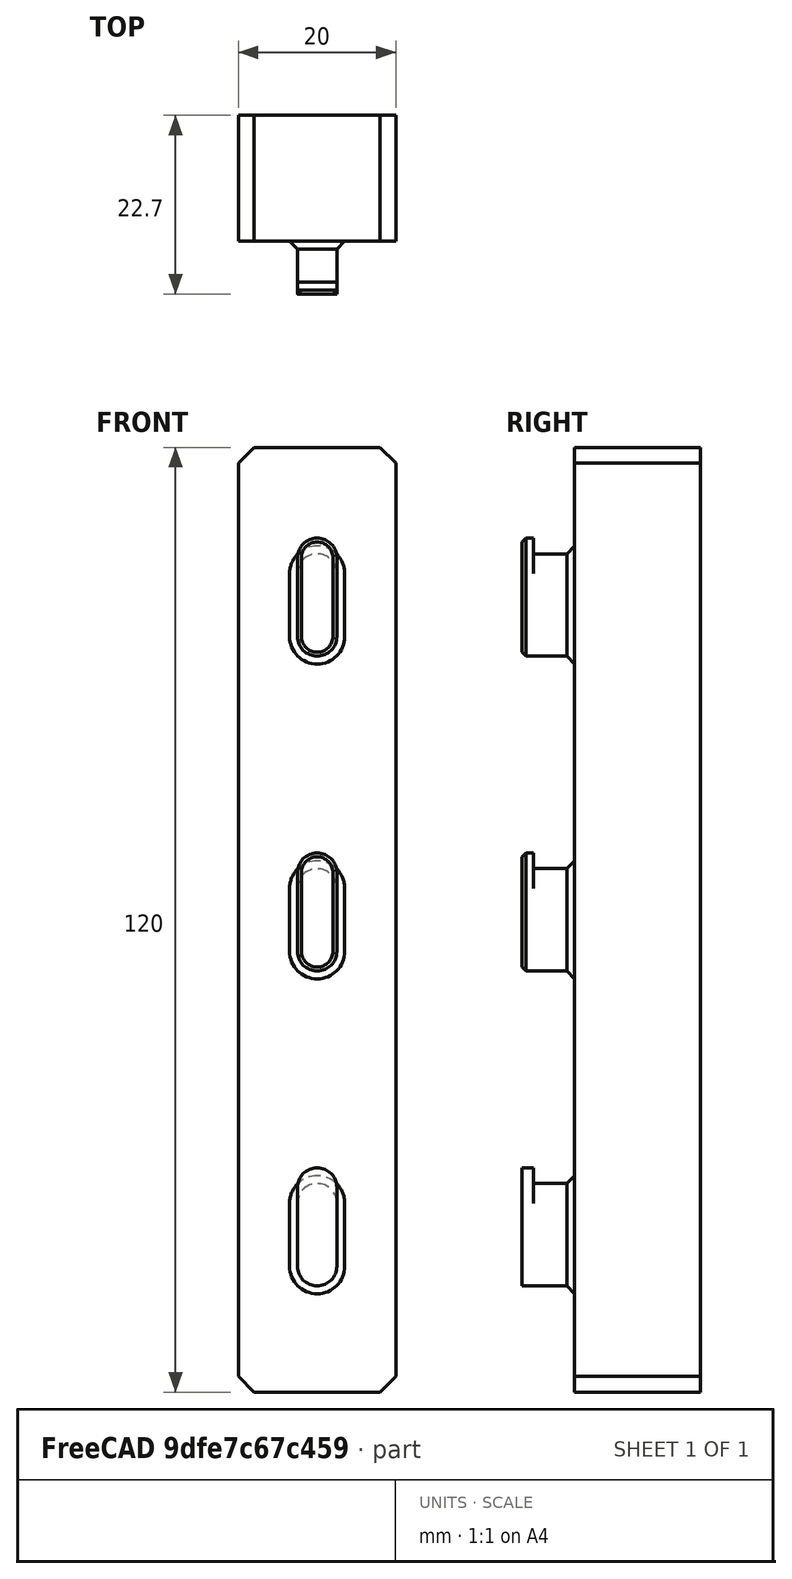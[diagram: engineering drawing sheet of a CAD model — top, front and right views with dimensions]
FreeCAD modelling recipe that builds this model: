
FCSTD DOCUMENT  (FreeCAD 1.0R39109 (Git))
Label: VertSkadis
License: All rights reserved
LicenseURL: http://en.wikipedia.org/wiki/All_rights_reserved
objects: PartDesign::Chamfer×3, Sketcher::SketchObject×2, PartDesign::Pad×2, PartDesign::AdditiveBox×1, PartDesign::Body×1, PartDesign::LinearPattern×1
note: 25 computed .brp shape members not serialized (recipe doc carries the construction recipe); baked Part::Feature solids carry a one-line shape summary decoded from their .brp

FEATURE [Sketcher::SketchObject] Sketch
  ArcFitTolerance = 1e-06
  AttachmentOffset = pos=(0,-40,0) rot=(0,0,1;0rad)
  AttachmentSupport = -> [XZ_Plane]
  FullyConstrained = true
  MakeInternals = false
  MapMode = 5
  Placement = pos=(0,-8.9e-15,-40) rot=(1,0,0;1.5708rad)
  sketch-geometry (4):
    g0: ArcOfCircle CenterX=1e-16 CenterY=4 CenterZ=0 NormalX=0 NormalY=0 NormalZ=1 AngleXU=0 Radius=2.5 StartAngle=4.39e-14 EndAngle=3.14159
    g1: ArcOfCircle CenterX=-1e-16 CenterY=-4 CenterZ=0 NormalX=0 NormalY=0 NormalZ=1 AngleXU=0 Radius=2.5 StartAngle=3.14159 EndAngle=6.28319
    g2: LineSegment StartX=2.5 StartY=4 StartZ=0 EndX=2.5 EndY=-4 EndZ=0
    g3: LineSegment StartX=-2.5 StartY=4 StartZ=0 EndX=-2.5 EndY=-4 EndZ=0
  constraints (9):
    c: Tangent(g0,g2) = 1.5708
    c: Tangent(g0,g3) = -1.5708
    c: Tangent(g1,g2) = 1.5708
    c: Tangent(g1,g3) = -1.5708
    c: Equal(g0,g1)
    c: Vertical(g2)
    c: DistanceX(g0,g0) = 5
    c: DistanceY(g1,g0) = 8
    c: Symmetric(g0,g1,g-1)
FEATURE [PartDesign::AdditiveBox] Box
  AttacherType = Attacher::AttachEngine3D
  AttachmentOffset = pos=(-60,-10,-16) rot=(0,0,1;0rad)
  AttachmentSupport = -> [Z_Axis]
  Height = 16
  Length = 120
  MapMode = 2
  Placement = pos=(10,16,-60) rot=(0.57735,-0.57735,0.57735;2.0944rad)
  Suppressed = false
  Width = 20
FEATURE [PartDesign::Pad] Pad
  BaseFeature = -> Box
  Direction = (0,-1,2e-16)
  Length = 5.2
  Length2 = 10
  Placement = pos=(10,16,-60) rot=(0.57735,-0.57735,0.57735;2.0944rad)
  Profile = -> Sketch
  ReferenceAxis = -> Sketch [N_Axis]
  Suppressed = false
  Type = 0
FEATURE [PartDesign::Chamfer] Chamfer
  Angle = 45
  Base = -> Pad [Edge13]
  BaseFeature = -> Pad
  ChamferType = 0
  FlipDirection = false
  Placement = pos=(10,16,-60) rot=(0.57735,-0.57735,0.57735;2.0944rad)
  Size = 1
  Size2 = 1
  SupportTransform = false
  Suppressed = false
  UseAllEdges = false
FEATURE [PartDesign::Body] Body
  AllowCompound = false
  Group = -> [Sketch,Box,Pad,Chamfer,LinearPattern,Sketch001,Pad001,Chamfer003,Chamfer001]
  Origin = -> Origin
  Tip = -> Chamfer003
FEATURE [PartDesign::LinearPattern] LinearPattern
  BaseFeature = -> Chamfer
  Direction = -> Sketch [V_Axis]
  Length = 80
  Mode = 1
  Occurrences = 3
  Offset = 40
  Originals = -> [Chamfer,Pad,Pad001,Chamfer001]
  Placement = pos=(10,16,-60) rot=(0.57735,-0.57735,0.57735;2.0944rad)
  Suppressed = false
  TransformMode = 0
FEATURE [Sketcher::SketchObject] Sketch001
  ArcFitTolerance = 1e-06
  AttachmentSupport = -> [LinearPattern]
  ExternalGeometry = -> [LinearPattern]
  FullyConstrained = true
  MakeInternals = false
  MapMode = 5
  Placement = pos=(10,-5.2,-60) rot=(0.57735,-0.57735,0.57735;2.0944rad)
  sketch-geometry (4):
    g0: ArcOfCircle CenterX=16 CenterY=10 CenterZ=0 NormalX=0 NormalY=0 NormalZ=1 AngleXU=0 Radius=2.5 StartAngle=1.5708 EndAngle=4.71239
    g1: ArcOfCircle CenterX=26 CenterY=10 CenterZ=0 NormalX=0 NormalY=0 NormalZ=1 AngleXU=0 Radius=2.5 StartAngle=4.71239 EndAngle=7.85398
    g2: LineSegment StartX=16 StartY=12.5 StartZ=0 EndX=26 EndY=12.5 EndZ=0
    g3: LineSegment StartX=16 StartY=7.5 StartZ=0 EndX=26 EndY=7.5 EndZ=0
  constraints (8):
    c: Tangent(g0,g2) = 1.5708
    c: Tangent(g0,g3) = -1.5708
    c: Tangent(g1,g2) = 1.5708
    c: Tangent(g1,g3) = -1.5708
    c: Equal(g0,g1)
    c: Coincident(g0,g-3)
    c: Coincident(g0,g-5)
    c: DistanceX(g-4,g1) = 2
FEATURE [PartDesign::Pad] Pad001
  BaseFeature = -> LinearPattern
  Direction = (0,-1,0)
  Length = 1.5
  Length2 = 10
  Placement = pos=(10,16,-60) rot=(0.57735,-0.57735,0.57735;2.0944rad)
  Profile = -> Sketch001
  ReferenceAxis = -> Sketch001 [N_Axis]
  Refine = true
  Suppressed = false
  Type = 0
FEATURE [PartDesign::Chamfer] Chamfer001
  Angle = 45
  Base = -> Chamfer003 [Edge88]
  BaseFeature = -> Chamfer003
  ChamferType = 0
  FlipDirection = false
  Placement = pos=(10,16,-60) rot=(0.57735,-0.57735,0.57735;2.0944rad)
  Size = 0.5
  Size2 = 1
  SupportTransform = false
  Suppressed = false
  UseAllEdges = false
FEATURE [PartDesign::Chamfer] Chamfer003
  Angle = 45
  Base = -> Pad001 [Edge41,Edge42,Edge45,Edge47]
  BaseFeature = -> Pad001
  ChamferType = 0
  FlipDirection = false
  Placement = pos=(10,16,-60) rot=(0.57735,-0.57735,0.57735;2.0944rad)
  Size = 2
  Size2 = 1
  SupportTransform = false
  Suppressed = false
  UseAllEdges = false
